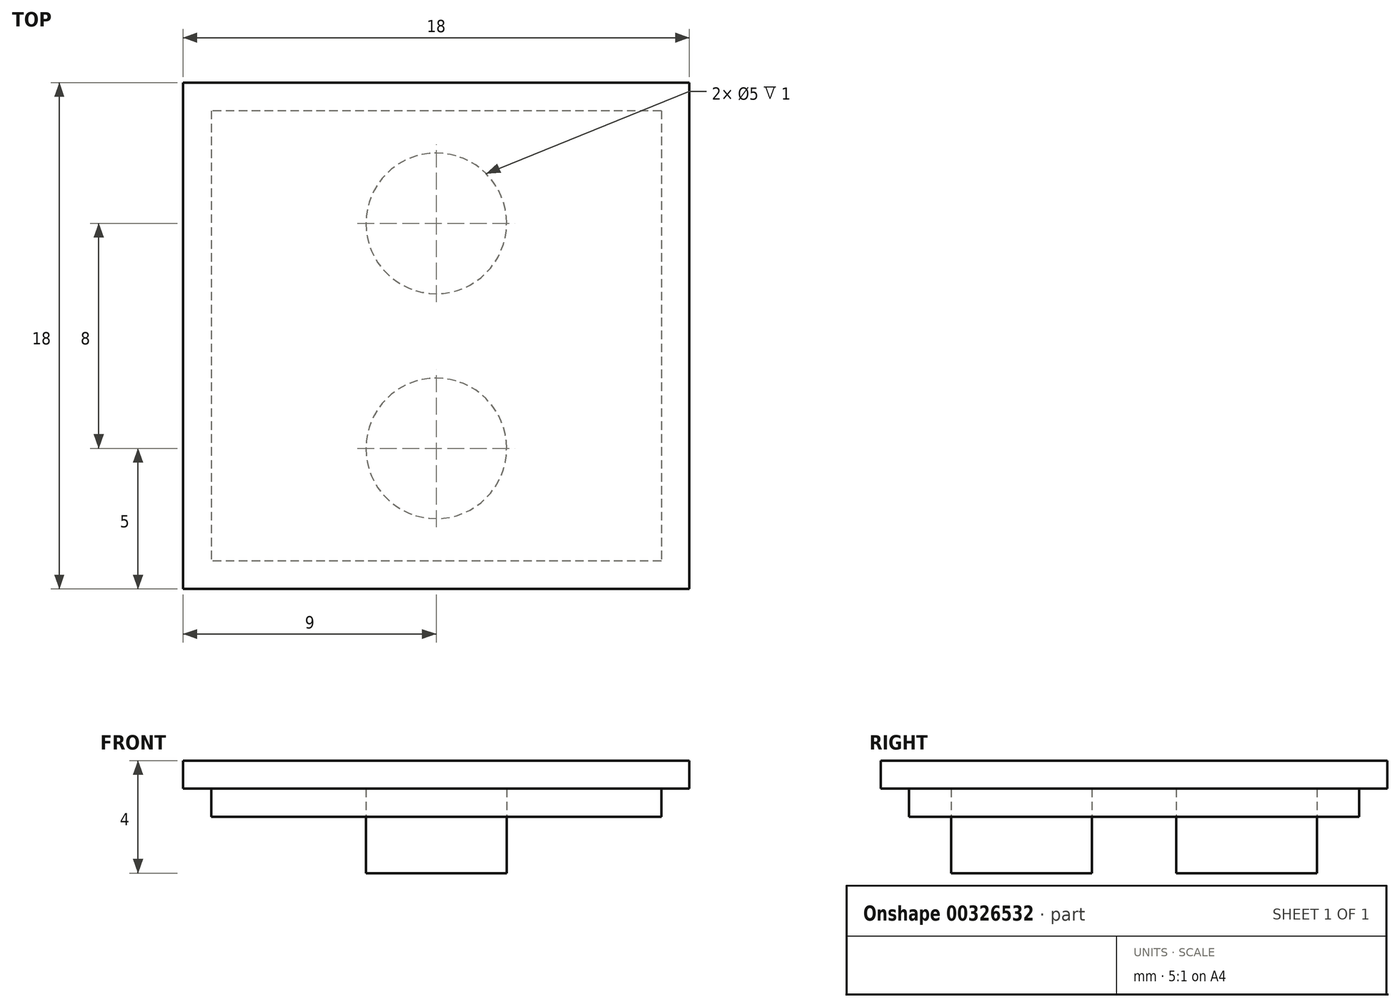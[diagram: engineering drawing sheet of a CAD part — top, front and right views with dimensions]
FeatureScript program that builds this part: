
annotation { "Feature Type Name" : "Feature", "Feature Type Description" : "" }
export const myFeature = defineFeature(function(context is Context, id is Id, definition is map)
    precondition{}
    {
        {
            var Q0;
            Q0=qCreatedBy(makeId("Top.planeOp"),FACE);
            var sketch = newSketch(context, id + "F0", { "sketchPlane" : qUnion([Q0])});
            skLineSegment(sketch, "E0.bottom", {"start": v(9, 9) * mm, "end": v(-9, 9) * mm});
            skLineSegment(sketch, "E0.top", {"start": v(9, -9) * mm, "end": v(-9, -9) * mm});
            skLineSegment(sketch, "E0.left", {"start": v(9, 9) * mm, "end": v(9, -9) * mm});
            skLineSegment(sketch, "E0.right", {"start": v(-9, 9) * mm, "end": v(-9, -9) * mm});
            skPoint(sketch, "E0.middle", {"position": v(0, 0) * mm});
            skLineSegment(sketch, "E1.0", {"start": v(-8, 8) * mm, "end": v(-8, -8) * mm});
            skLineSegment(sketch, "E1.1", {"start": v(8, 8) * mm, "end": v(-8, 8) * mm});
            skLineSegment(sketch, "E1.2", {"start": v(8, 8) * mm, "end": v(8, -8) * mm});
            skLineSegment(sketch, "E1.3", {"start": v(8, -8) * mm, "end": v(-8, -8) * mm});
            skLineSegment(sketch, "E2", {"start": v(0, 0) * mm, "end": v(0, 8) * mm, "construction": true});
            skLineSegment(sketch, "E3", {"start": v(0, 0) * mm, "end": v(0, -8) * mm, "construction": true});
            skPoint(sketch, "E4", {"position": v(0, 4) * mm});
            skPoint(sketch, "E5", {"position": v(0, -4) * mm});
            skCircle(sketch, "E6", {"center": v(0, 4) * mm, "radius": 2.5 * mm});
            skCircle(sketch, "E7", {"center": v(0, -4) * mm, "radius": 2.5 * mm});
            skSolve(sketch);
        }
        {
            var Q0;
            Q0=makeQuery(id+"F0.imprint","IMPRINT",FACE,{"disambiguationData":[TD([[makeQuery(id+"F0.imprint","IMPRINT",EDGE,{"derivedFrom":sQuery(id+"F0.wireOp",EDGE,"E1.0")}),1.0]])]});
            var Q1;
            Q1=makeQuery(id+"F0.imprint","IMPRINT",FACE,{"disambiguationData":[TD([[makeQuery(id+"F0.imprint","IMPRINT",EDGE,{"derivedFrom":sQuery(id+"F0.wireOp",EDGE,"E6")}),1.0]])]});
            var Q2;
            Q2=makeQuery(id+"F0.imprint","IMPRINT",FACE,{"disambiguationData":[TD([[makeQuery(id+"F0.imprint","IMPRINT",EDGE,{"derivedFrom":sQuery(id+"F0.wireOp",EDGE,"E7")}),1.0]])]});
            var Q3;
            Q3=makeQuery(id+"F0.imprint","IMPRINT",FACE,{"disambiguationData":[TD([[makeQuery(id+"F0.imprint","IMPRINT",EDGE,{"derivedFrom":sQuery(id+"F0.wireOp",EDGE,"E0.bottom")}),1.0]])]});
            extrude(context, id + "F1", {"entities" : qUnion([Q0, Q1, Q2, Q3]), "depth" : 2 * mm});
        }
        {
            var Q0;
            Q0=makeQuery(id+"F0.imprint","IMPRINT",FACE,{"disambiguationData":[TD([[makeQuery(id+"F0.imprint","IMPRINT",EDGE,{"derivedFrom":sQuery(id+"F0.wireOp",EDGE,"E0.bottom")}),1.0]])]});
            extrude(context, id + "F2", {"entities" : qUnion([Q0]), "operationType" : NewBodyOperationType.REMOVE, "depth" : 1 * mm});
        }
        {
            var Q0;
            Q0=makeQuery(id+"F0.imprint","IMPRINT",FACE,{"disambiguationData":[TD([[makeQuery(id+"F0.imprint","IMPRINT",EDGE,{"derivedFrom":sQuery(id+"F0.wireOp",EDGE,"E7")}),1.0]])]});
            var Q1;
            Q1=makeQuery(id+"F0.imprint","IMPRINT",FACE,{"disambiguationData":[TD([[makeQuery(id+"F0.imprint","IMPRINT",EDGE,{"derivedFrom":sQuery(id+"F0.wireOp",EDGE,"E6")}),1.0]])]});
            extrude(context, id + "F3", {"entities" : qUnion([Q0, Q1]), "operationType" : NewBodyOperationType.REMOVE, "depth" : 1 * mm});
        }
        {
            var Q0;
            Q0=makeQuery(id+"F0.imprint","IMPRINT",FACE,{"disambiguationData":[TD([[makeQuery(id+"F0.imprint","IMPRINT",EDGE,{"derivedFrom":sQuery(id+"F0.wireOp",EDGE,"E7")}),1.0]])]});
            var Q1;
            Q1=makeQuery(id+"F0.imprint","IMPRINT",FACE,{"disambiguationData":[TD([[makeQuery(id+"F0.imprint","IMPRINT",EDGE,{"derivedFrom":sQuery(id+"F0.wireOp",EDGE,"E6")}),1.0]])]});
            extrude(context, id + "F4", {"entities" : qUnion([Q0, Q1]), "oppositeDirection" : true, "depth" : 2 * mm});
        }
    });
